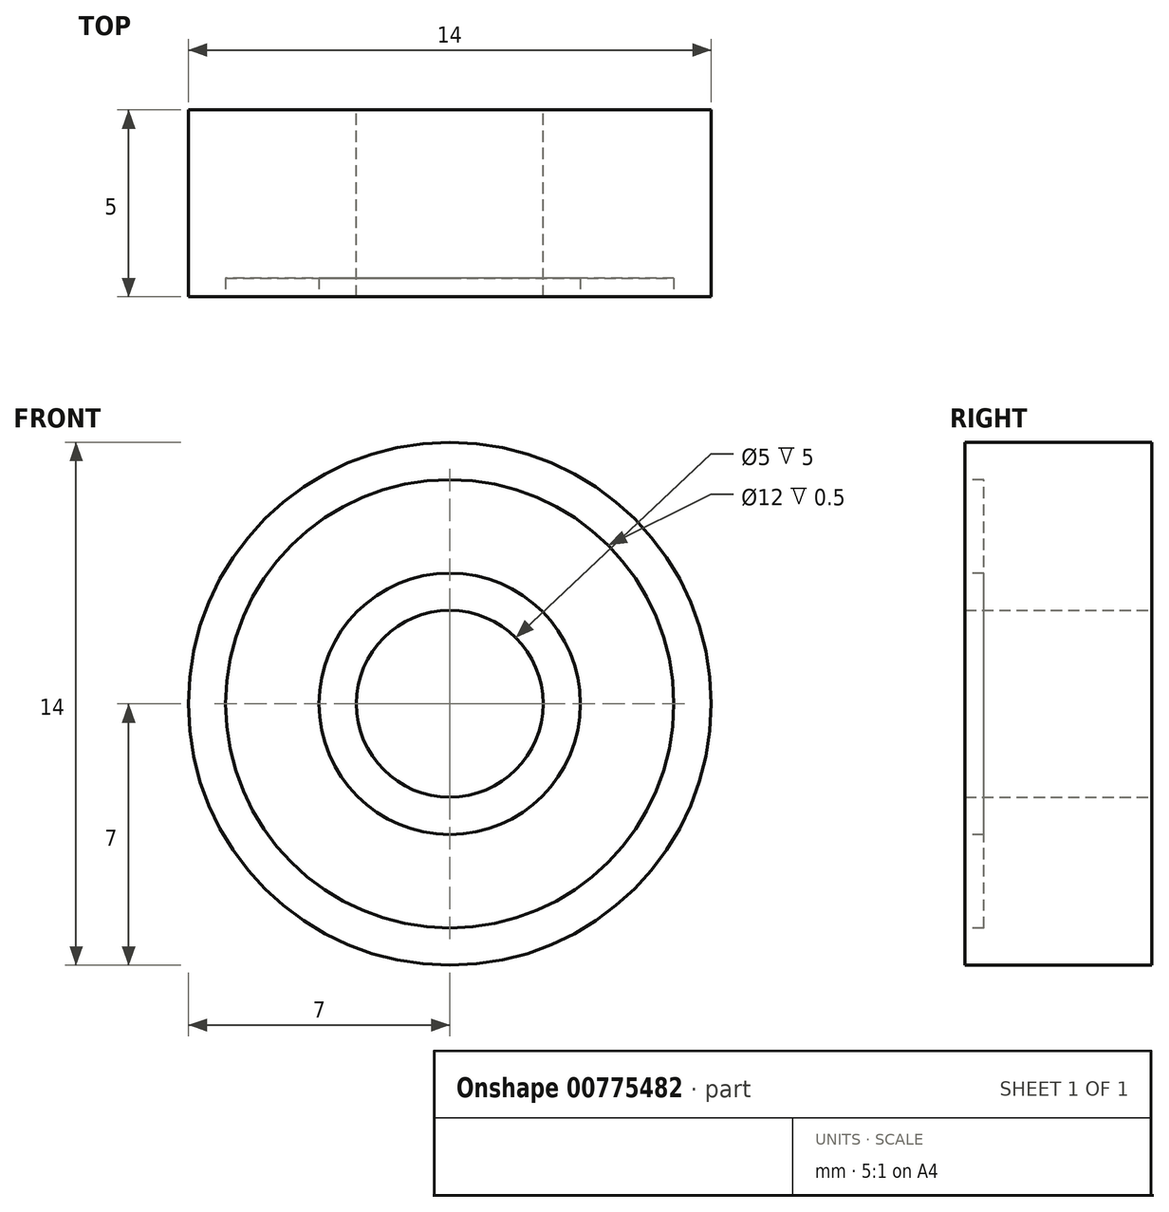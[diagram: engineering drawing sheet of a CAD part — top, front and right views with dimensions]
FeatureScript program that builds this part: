
annotation { "Feature Type Name" : "Feature", "Feature Type Description" : "" }
export const myFeature = defineFeature(function(context is Context, id is Id, definition is map)
    precondition{}
    {
        {
            var Q0;
            Q0=qCreatedBy(makeId("Front.planeOp"),FACE);
            var sketch = newSketch(context, id + "F0", { "sketchPlane" : qUnion([Q0])});
            skCircle(sketch, "E0", {"center": v(0, 0) * mm, "radius": 2.5 * mm});
            skCircle(sketch, "E1", {"center": v(0, 0) * mm, "radius": 7 * mm});
            skSolve(sketch);
        }
        {
            var Q0;
            Q0=makeQuery(id+"F0.imprint","IMPRINT",FACE,{"disambiguationData":[TD([[makeQuery(id+"F0.imprint","IMPRINT",EDGE,{"derivedFrom":sQuery(id+"F0.wireOp",EDGE,"E0")}),-1.0]])]});
            extrude(context, id + "F1", {"entities" : qUnion([Q0]), "endBound" : BoundingType.SYMMETRIC, "depth" : 5 * mm, "offsetDistance" : 25 * mm});
        }
        {
            var Q0;
            Q0=makeQuery(id+"F1.opExtrude","CAP_FACE",FACE,{"disambiguationData":[OSD([sQuery(id+"F0.wireOp",EDGE,"E0"),sQuery(id+"F0.wireOp",EDGE,"E1")])],"isStart":false});
            var sketch = newSketch(context, id + "F2", { "sketchPlane" : qUnion([Q0])});
            skCircle(sketch, "E2.0", {"center": v(0, 0) * mm, "radius": 6 * mm});
            skCircle(sketch, "E3.0", {"center": v(0, 0) * mm, "radius": 3.5 * mm});
            skSolve(sketch);
        }
        {
            var Q0;
            Q0=makeQuery(id+"F2.imprint","IMPRINT",FACE,{"disambiguationData":[TD([[makeQuery(id+"F2.imprint","IMPRINT",EDGE,{"derivedFrom":sQuery(id+"F2.wireOp",EDGE,"E2.0")}),1.0]])]});
            extrude(context, id + "F3", {"entities" : qUnion([Q0]), "operationType" : NewBodyOperationType.REMOVE, "oppositeDirection" : true, "depth" : 1.5 * mm, "offsetDistance" : 25 * mm});
        }
        {
            var Q0;
            Q0=makeQuery(id+"F3.boolean.opBoolean","COPY",FACE,{"derivedFrom":makeQuery(id+"F3.opExtrude","CAP_FACE",FACE,{"disambiguationData":[OSD([sQuery(id+"F2.wireOp",EDGE,"E2.0"),sQuery(id+"F2.wireOp",EDGE,"E3.0")])],"isStart":false})});
            extrude(context, id + "F4", {"entities" : qUnion([Q0]), "depth" : 1 * mm, "offsetDistance" : 25 * mm});
        }
        {
            var Q0;
            Q0=makeQuery(id+"F4.opExtrude","SWEPT_BODY",BODY,{"disambiguationData":[OSD([sQuery(id+"F2.wireOp",EDGE,"E2.0"),sQuery(id+"F2.wireOp",EDGE,"E3.0")])]});
            var Q1;
            Q1=qCreatedBy(makeId("Front.planeOp"),FACE);
            mirror(context, id + "F5", {"operationType" : NewBodyOperationType.ADD, "entities" : qUnion([Q0]), "mirrorPlane" : qUnion([Q1])});
        }
    });
